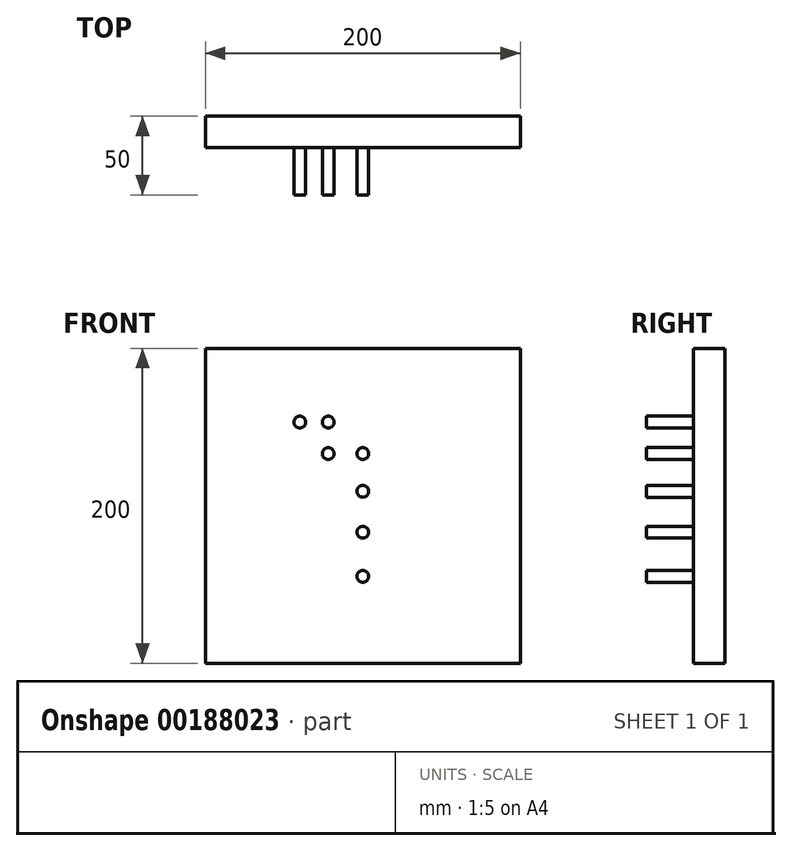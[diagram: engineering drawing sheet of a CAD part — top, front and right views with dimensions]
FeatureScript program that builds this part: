
annotation { "Feature Type Name" : "Feature", "Feature Type Description" : "" }
export const myFeature = defineFeature(function(context is Context, id is Id, definition is map)
    precondition{}
    {
        {
            var Q0;
            Q0=qCreatedBy(makeId("Front.planeOp"),FACE);
            var sketch = newSketch(context, id + "F0", { "sketchPlane" : qUnion([Q0])});
            skLineSegment(sketch, "E0.bottom", {"start": v(100, 100) * mm, "end": v(-100, 100) * mm});
            skLineSegment(sketch, "E0.top", {"start": v(100, -100) * mm, "end": v(-100, -100) * mm});
            skLineSegment(sketch, "E0.left", {"start": v(100, 100) * mm, "end": v(100, -100) * mm});
            skLineSegment(sketch, "E0.right", {"start": v(-100, 100) * mm, "end": v(-100, -100) * mm});
            skPoint(sketch, "E0.middle", {"position": v(0, 0) * mm});
            skSolve(sketch);
        }
        {
            var Q0;
            Q0=makeQuery(id+"F0.imprint","IMPRINT",FACE,{"disambiguationData":[TD([[makeQuery(id+"F0.imprint","IMPRINT",EDGE,{"derivedFrom":sQuery(id+"F0.wireOp",EDGE,"E0.bottom")}),1.0]])]});
            extrude(context, id + "F1", {"entities" : qUnion([Q0]), "depth" : 20 * mm});
        }
        {
            var Q0;
            Q0=makeQuery(id+"F1.opExtrude","CAP_FACE",FACE,{"disambiguationData":[OSD([sQuery(id+"F0.wireOp",EDGE,"E0.bottom"),sQuery(id+"F0.wireOp",EDGE,"E0.top"),sQuery(id+"F0.wireOp",EDGE,"E0.left"),sQuery(id+"F0.wireOp",EDGE,"E0.right")])],"isStart":false});
            var sketch = newSketch(context, id + "F2", { "sketchPlane" : qUnion([Q0])});
            skCircle(sketch, "E1", {"center": v(-40, 53.21) * mm, "radius": 3.75 * mm});
            skCircle(sketch, "E2", {"center": v(-22, 53.21) * mm, "radius": 3.75 * mm});
            skCircle(sketch, "E3", {"center": v(-22, 33.21) * mm, "radius": 3.75 * mm});
            skCircle(sketch, "E4", {"center": v(0, 33.21) * mm, "radius": 3.75 * mm});
            skCircle(sketch, "E5", {"center": v(0, 9.21) * mm, "radius": 3.75 * mm});
            skCircle(sketch, "E6", {"center": v(0, -16.79) * mm, "radius": 3.75 * mm});
            skCircle(sketch, "E7", {"center": v(0, -44.79) * mm, "radius": 3.75 * mm});
            skSolve(sketch);
        }
        {
            var Q0;
            Q0=qSketchRegion(id+"F2",true);
            extrude(context, id + "F3", {"entities" : qUnion([Q0]), "operationType" : NewBodyOperationType.ADD, "depth" : 30 * mm});
        }
    });
